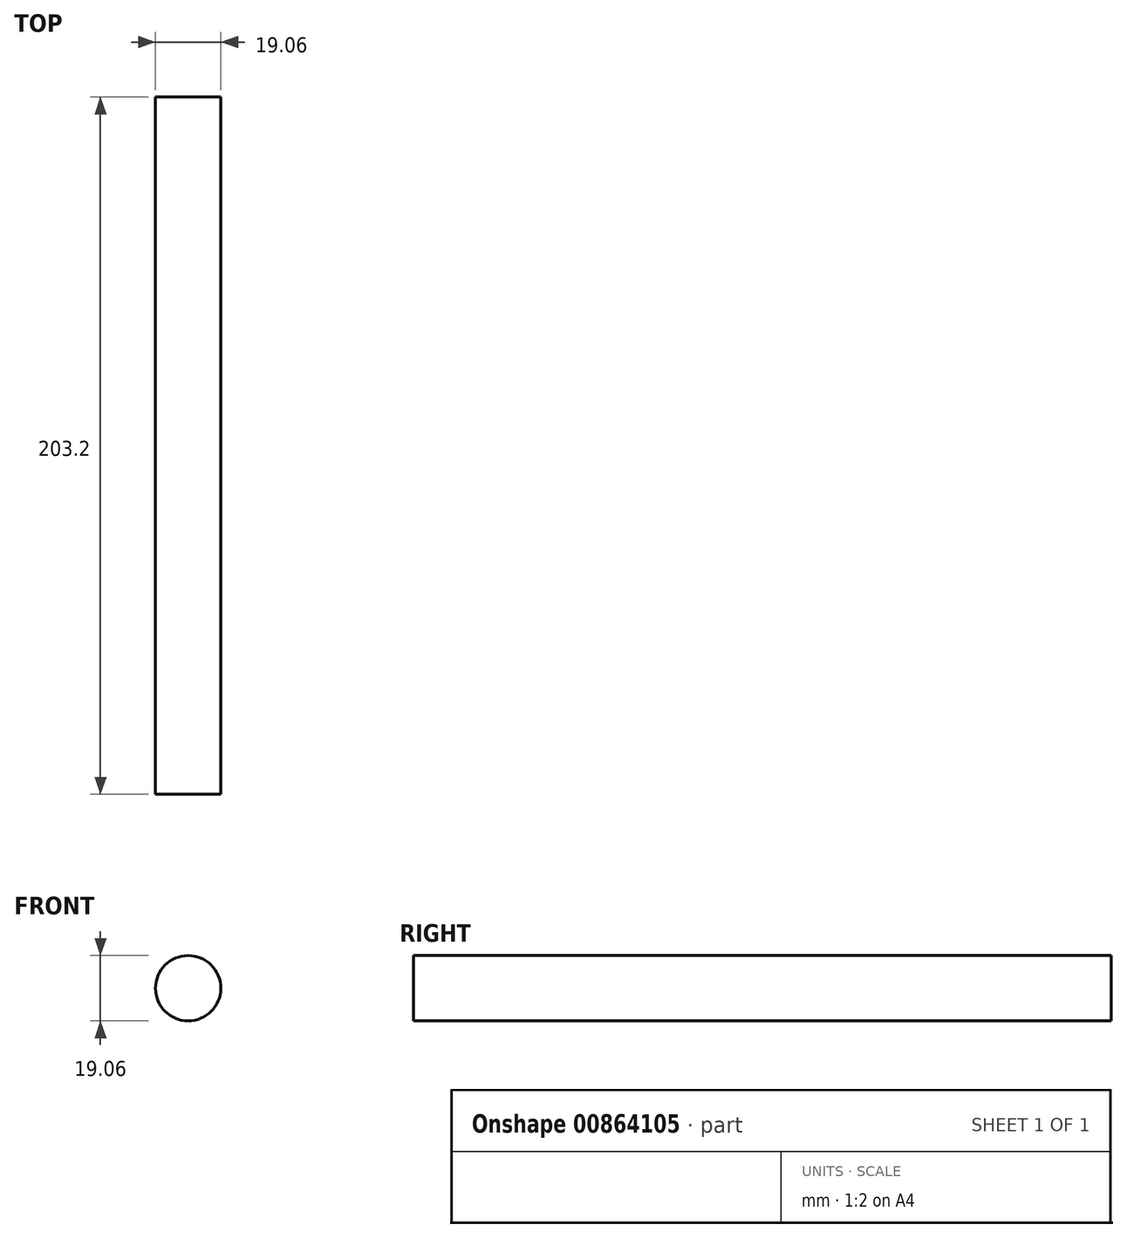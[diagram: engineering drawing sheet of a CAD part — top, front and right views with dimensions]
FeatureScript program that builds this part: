
annotation { "Feature Type Name" : "Feature", "Feature Type Description" : "" }
export const myFeature = defineFeature(function(context is Context, id is Id, definition is map)
    precondition{}
    {
        {
            var Q0;
            Q0=qCreatedBy(makeId("Front.planeOp"),FACE);
            var sketch = newSketch(context, id + "F0", { "sketchPlane" : qUnion([Q0])});
            skCircle(sketch, "E0", {"center": v(0, 0) * mm, "radius": 9.53 * mm});
            skSolve(sketch);
        }
        {
            var Q0;
            Q0=makeQuery(id+"F0.imprint","IMPRINT",FACE,{"disambiguationData":[TD([[makeQuery(id+"F0.imprint","IMPRINT",EDGE,{"derivedFrom":sQuery(id+"F0.wireOp",EDGE,"E0")}),1.0]])]});
            extrude(context, id + "F1", {"entities" : qUnion([Q0]), "depth" : 203.2 * mm, "offsetDistance" : 25.4 * mm});
        }
    });
